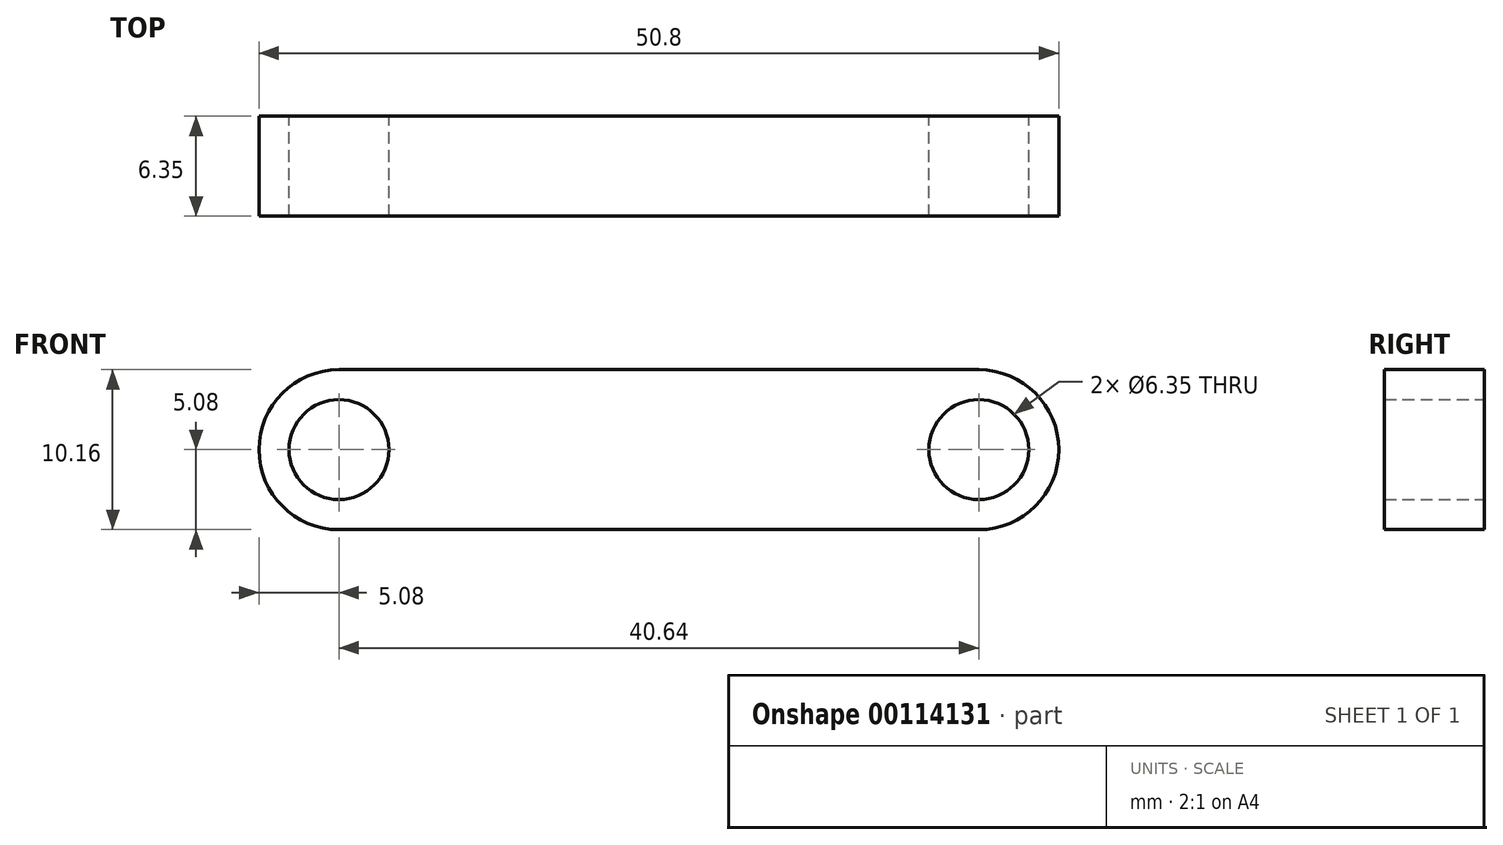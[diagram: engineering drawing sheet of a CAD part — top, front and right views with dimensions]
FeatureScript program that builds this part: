
annotation { "Feature Type Name" : "Feature", "Feature Type Description" : "" }
export const myFeature = defineFeature(function(context is Context, id is Id, definition is map)
    precondition{}
    {
        {
            var Q0;
            Q0=qCreatedBy(makeId("Front.planeOp"),FACE);
            var sketch = newSketch(context, id + "F0", { "sketchPlane" : qUnion([Q0])});
            skLineSegment(sketch, "E0.bottom", {"start": v(20.32, -5.08) * mm, "end": v(-20.32, -5.08) * mm});
            skLineSegment(sketch, "E0.top", {"start": v(20.32, 5.08) * mm, "end": v(-20.32, 5.08) * mm});
            skLineSegment(sketch, "E0.left", {"start": v(25.4, 0) * mm, "end": v(25.4, 0) * mm});
            skLineSegment(sketch, "E0.right", {"start": v(-25.4, 0) * mm, "end": v(-25.4, 0) * mm});
            skPoint(sketch, "E0.middle", {"position": v(0, 0) * mm});
            skPoint(sketch, "E1.visualSharp", {"position": v(-25.4, 5.08) * mm});
            skArc(sketch, "E1.filletArc", {"start": v(-20.32, 5.08) * mm, "mid": v(-23.91, 3.6) * mm, "end": v(-25.4, 0) * mm});
            skPoint(sketch, "E2.visualSharp", {"position": v(-25.4, -5.08) * mm});
            skArc(sketch, "E2.filletArc", {"start": v(-25.4, 0) * mm, "mid": v(-23.91, -3.6) * mm, "end": v(-20.32, -5.08) * mm});
            skPoint(sketch, "E3.visualSharp", {"position": v(25.4, 5.08) * mm});
            skArc(sketch, "E3.filletArc", {"start": v(25.4, 0) * mm, "mid": v(23.91, 3.6) * mm, "end": v(20.32, 5.08) * mm});
            skPoint(sketch, "E4.visualSharp", {"position": v(25.4, -5.08) * mm});
            skArc(sketch, "E4.filletArc", {"start": v(20.32, -5.08) * mm, "mid": v(23.91, -3.6) * mm, "end": v(25.4, 0) * mm});
            skCircle(sketch, "E5", {"center": v(-20.32, 0) * mm, "radius": 3.18 * mm});
            skCircle(sketch, "E6", {"center": v(20.32, 0) * mm, "radius": 3.18 * mm});
            skSolve(sketch);
        }
        {
            var Q0;
            Q0=makeQuery(id+"F0.imprint","IMPRINT",FACE,{"disambiguationData":[TD([[makeQuery(id+"F0.imprint","IMPRINT",EDGE,{"derivedFrom":sQuery(id+"F0.wireOp",EDGE,"E0.bottom")}),-1.0]])]});
            extrude(context, id + "F1", {"entities" : qUnion([Q0]), "depth" : 6.35 * mm});
        }
    });
